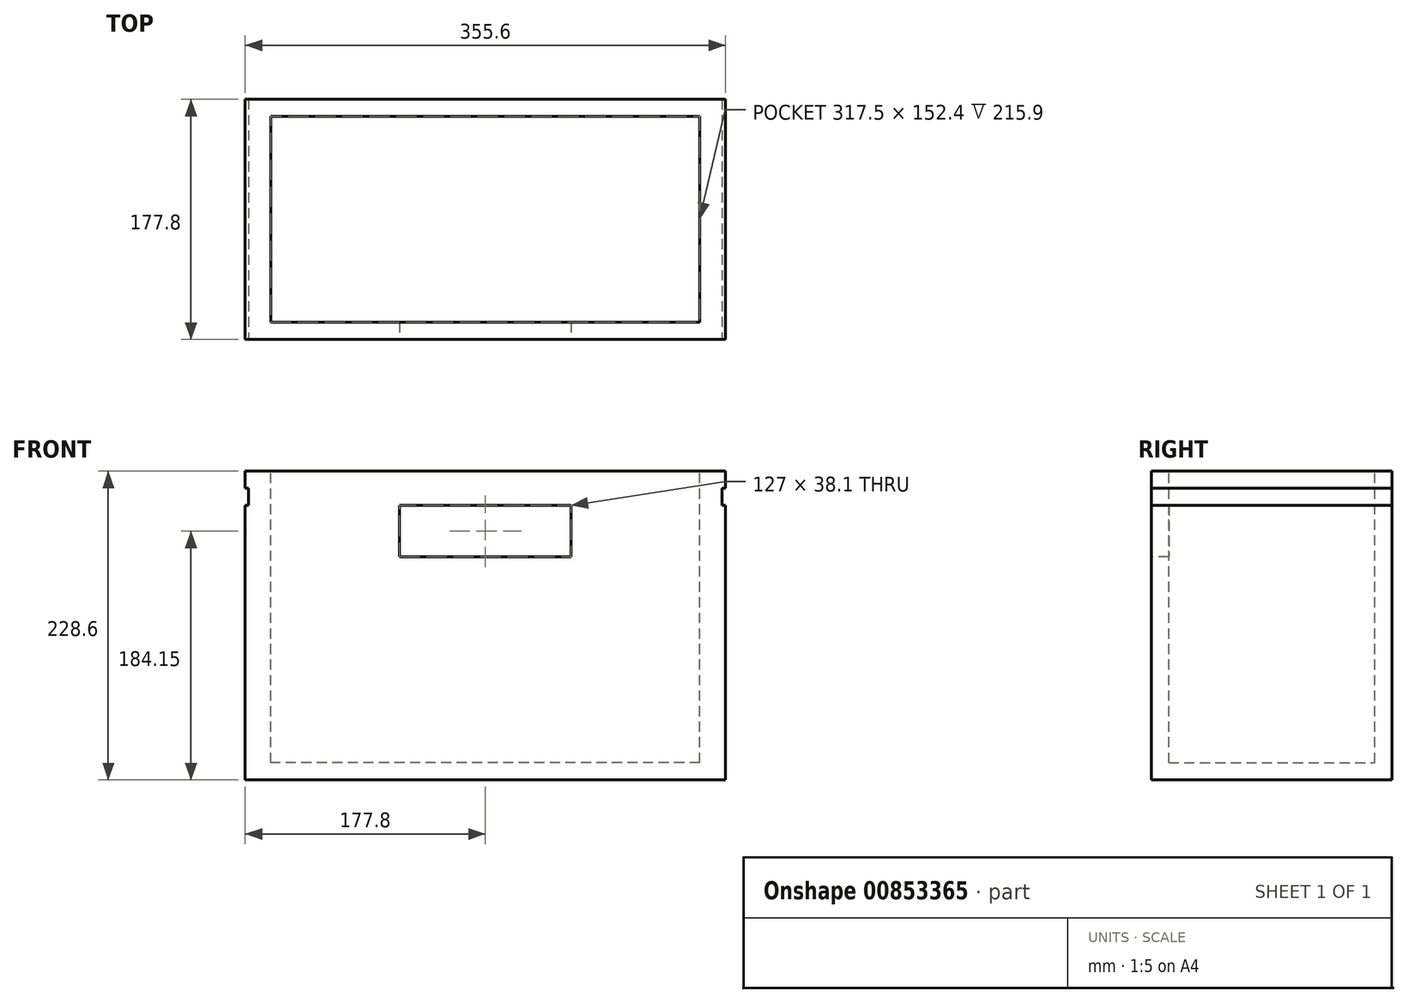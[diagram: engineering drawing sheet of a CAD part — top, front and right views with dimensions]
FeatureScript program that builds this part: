
annotation { "Feature Type Name" : "Feature", "Feature Type Description" : "" }
export const myFeature = defineFeature(function(context is Context, id is Id, definition is map)
    precondition{}
    {
        {
            var Q0;
            Q0=qCreatedBy(makeId("Front.planeOp"),FACE);
            var sketch = newSketch(context, id + "F0", { "sketchPlane" : qUnion([Q0])});
            skLineSegment(sketch, "E0.bottom", {"start": v(177.8, -114.3) * mm, "end": v(-177.8, -114.3) * mm});
            skLineSegment(sketch, "E0.top", {"start": v(177.8, 114.3) * mm, "end": v(-177.8, 114.3) * mm});
            skLineSegment(sketch, "E0.left", {"start": v(177.8, -114.3) * mm, "end": v(177.8, 114.3) * mm});
            skLineSegment(sketch, "E0.right", {"start": v(-177.8, -114.3) * mm, "end": v(-177.8, 114.3) * mm});
            skPoint(sketch, "E0.middle", {"position": v(0, 0) * mm});
            skSolve(sketch);
        }
        {
            var Q0;
            Q0 = qSketchRegion(id + "F0", true);
            extrude(context, id + "F1", {"entities" : qUnion([Q0]), "depth" : 177.8 * mm, "offsetDistance" : 25.4 * mm, "hasSecondDirection" : true, "secondDirectionOppositeDirection" : true, "secondDirectionDepth" : 0 * mm});
        }
        {
            var Q0;
            Q0=makeQuery(id+"F1.opExtrude","SWEPT_FACE",FACE,{"disambiguationData":[OSD([sQuery(id+"F0.wireOp",EDGE,"E0.top")])]});
            var sketch = newSketch(context, id + "F2", { "sketchPlane" : qUnion([Q0])});
            skLineSegment(sketch, "E1.bottom", {"start": v(158.75, -165.1) * mm, "end": v(-158.75, -165.1) * mm});
            skLineSegment(sketch, "E1.top", {"start": v(158.75, -12.7) * mm, "end": v(-158.75, -12.7) * mm});
            skLineSegment(sketch, "E1.left", {"start": v(158.75, -165.1) * mm, "end": v(158.75, -12.7) * mm});
            skLineSegment(sketch, "E1.right", {"start": v(-158.75, -165.1) * mm, "end": v(-158.75, -12.7) * mm});
            skPoint(sketch, "E1.middle", {"position": v(0, -88.9) * mm});
            skSolve(sketch);
        }
        {
            var Q0;
            Q0 = qSketchRegion(id + "F2", true);
            extrude(context, id + "F3", {"entities" : qUnion([Q0]), "operationType" : NewBodyOperationType.REMOVE, "oppositeDirection" : true, "depth" : 215.9 * mm, "offsetDistance" : 25.4 * mm});
        }
        {
            var Q0;
            Q0=makeQuery(id+"F1.opExtrude","CAP_FACE",FACE,{"disambiguationData":[OSD([sQuery(id+"F0.wireOp",EDGE,"E0.bottom"),sQuery(id+"F0.wireOp",EDGE,"E0.top"),sQuery(id+"F0.wireOp",EDGE,"E0.left"),sQuery(id+"F0.wireOp",EDGE,"E0.right")])],"isStart":false});
            var sketch = newSketch(context, id + "F4", { "sketchPlane" : qUnion([Q0])});
            skLineSegment(sketch, "E2.bottom", {"start": v(63.5, 50.8) * mm, "end": v(-63.5, 50.8) * mm});
            skLineSegment(sketch, "E2.top", {"start": v(63.5, 88.9) * mm, "end": v(-63.5, 88.9) * mm});
            skLineSegment(sketch, "E2.left", {"start": v(63.5, 50.8) * mm, "end": v(63.5, 88.9) * mm});
            skLineSegment(sketch, "E2.right", {"start": v(-63.5, 50.8) * mm, "end": v(-63.5, 88.9) * mm});
            skPoint(sketch, "E2.middle", {"position": v(0, 69.85) * mm});
            skPoint(sketch, "E2.middle.positionSnap0", {"position": v(0, -114.3) * mm});
            skPoint(sketch, "E2.centerSnap0", {"position": v(0, -114.3) * mm});
            skSolve(sketch);
        }
        {
            var Q0;
            Q0 = qSketchRegion(id + "F4", true);
            extrude(context, id + "F5", {"entities" : qUnion([Q0]), "operationType" : NewBodyOperationType.REMOVE, "oppositeDirection" : true, "depth" : 25.4 * mm, "offsetDistance" : 25.4 * mm});
        }
        {
            var Q0;
            Q0=makeQuery(id+"F1.opExtrude","CAP_FACE",FACE,{"disambiguationData":[OSD([sQuery(id+"F0.wireOp",EDGE,"E0.bottom"),sQuery(id+"F0.wireOp",EDGE,"E0.top"),sQuery(id+"F0.wireOp",EDGE,"E0.left"),sQuery(id+"F0.wireOp",EDGE,"E0.right")])],"isStart":false});
            var sketch = newSketch(context, id + "F6", { "sketchPlane" : qUnion([Q0])});
            skLineSegment(sketch, "E3.bottom", {"start": v(-177.8, 88.9) * mm, "end": v(-175.26, 88.9) * mm});
            skLineSegment(sketch, "E3.top", {"start": v(-177.8, 101.6) * mm, "end": v(-175.26, 101.6) * mm});
            skLineSegment(sketch, "E3.left", {"start": v(-177.8, 101.6) * mm, "end": v(-177.8, 88.9) * mm});
            skLineSegment(sketch, "E3.right", {"start": v(-175.26, 101.6) * mm, "end": v(-175.26, 88.9) * mm});
            skLineSegment(sketch, "E4.bottom", {"start": v(177.8, 88.9) * mm, "end": v(175.26, 88.9) * mm});
            skLineSegment(sketch, "E4.top", {"start": v(177.8, 101.6) * mm, "end": v(175.26, 101.6) * mm});
            skLineSegment(sketch, "E4.left", {"start": v(177.8, 101.6) * mm, "end": v(177.8, 88.9) * mm});
            skLineSegment(sketch, "E4.right", {"start": v(175.26, 101.6) * mm, "end": v(175.26, 88.9) * mm});
            skSolve(sketch);
        }
        {
            var Q0;
            Q0 = qSketchRegion(id + "F6", true);
            extrude(context, id + "F7", {"entities" : qUnion([Q0]), "operationType" : NewBodyOperationType.REMOVE, "endBound" : BoundingType.THROUGH_ALL, "oppositeDirection" : true, "depth" : 25.4 * mm, "offsetDistance" : 25.4 * mm});
        }
    });
